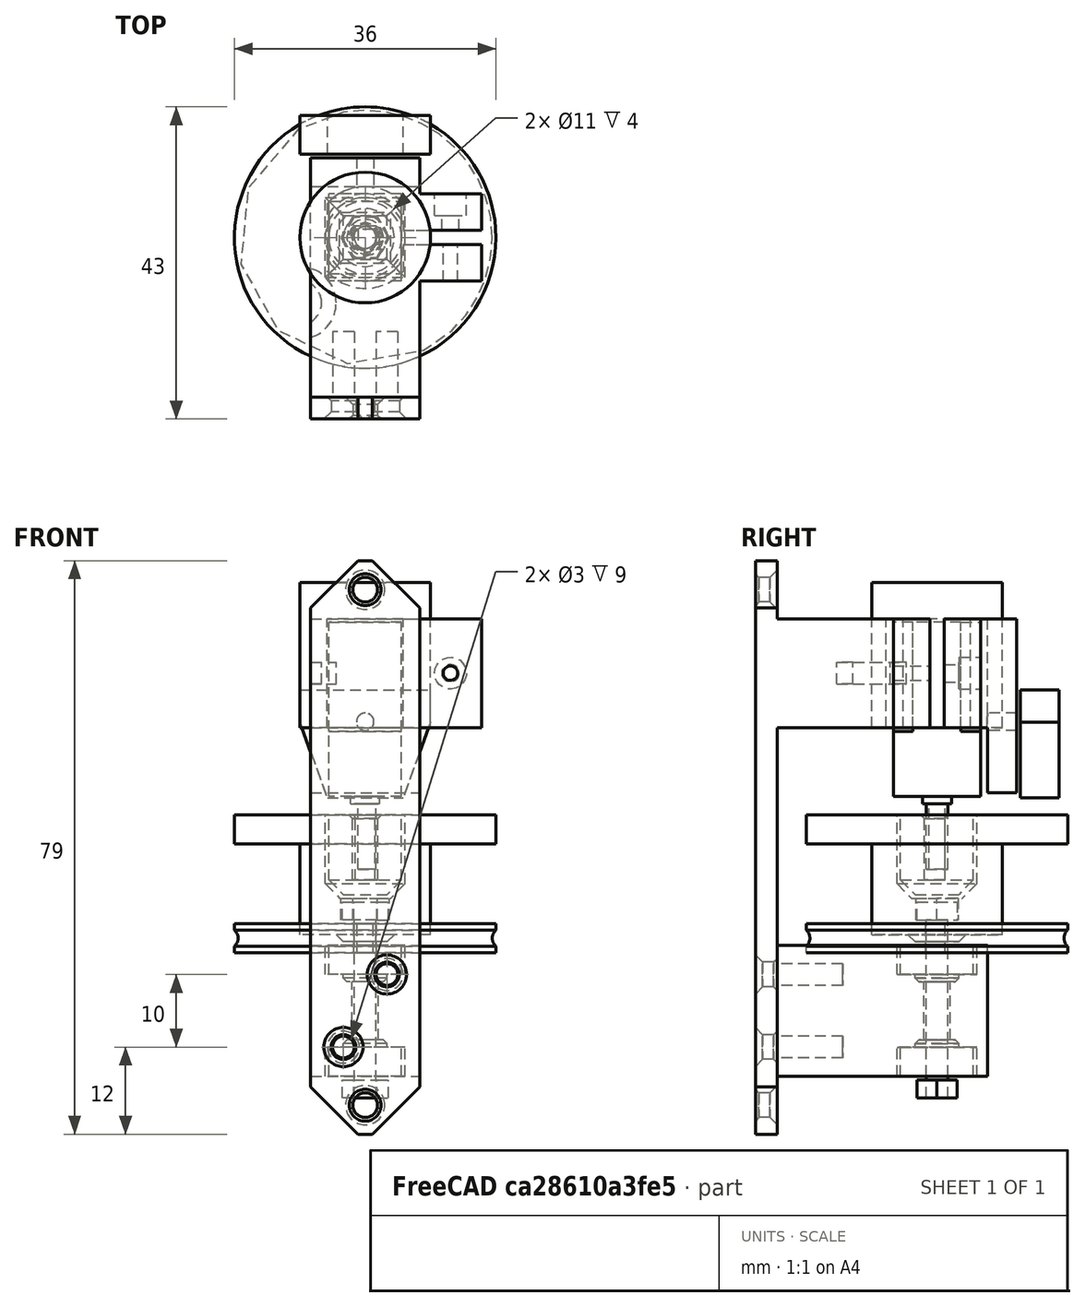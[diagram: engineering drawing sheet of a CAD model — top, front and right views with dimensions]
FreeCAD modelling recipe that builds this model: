
FCSTD DOCUMENT  (FreeCAD 0.18R16146 (Git))
Label: Motor and Opto Sensor Mount0.2
License: All rights reserved
LicenseURL: http://en.wikipedia.org/wiki/All_rights_reserved
objects: Part::Cylinder×31, Part::Cut×23, Part::Box×19, Part::MultiFuse×13, Part::Chamfer×10, Drawing::FeatureViewAnnotation×4, Part::Feature×3, Part::Fuse×3, Part::MultiCommon×2, Part::Torus×1, Part::Mirroring×1, Part::Cone×1, Drawing::FeaturePage×1
note: 107 computed .brp shape members not serialized (recipe doc carries the construction recipe); baked Part::Feature solids carry a one-line shape summary decoded from their .brp

FEATURE [Part::Box] Box406008004  label="gearbox004"
  AttacherType = Attacher::AttachEngine3D
  Height = 9
  Length = 12
  Placement = pos=(-6,-5,0) rot=(0,0,1;0rad)
  Width = 10
FEATURE [Part::Cylinder] Cylinder076  label="boss002"
  Angle = 360
  AttacherType = Attacher::AttachEngine3D
  Height = 1
  Placement = pos=(0,0,-1) rot=(0,0,1;0rad)
  Radius = 2
FEATURE [Part::Cylinder] Cylinder077
  Angle = 360
  AttacherType = Attacher::AttachEngine3D
  Height = 15
  Placement = pos=(0,0,9) rot=(0,0,1;0rad)
  Radius = 6
FEATURE [Part::Box] Box406008005  label="gearbox005"
  AttacherType = Attacher::AttachEngine3D
  Height = 27
  Length = 16
  Placement = pos=(-8,-5,0) rot=(0,0,1;0rad)
  Width = 10
FEATURE [Part::MultiCommon] Common001  label="motor002"
  Shapes = -> [Cylinder077,Box406008005]
FEATURE [Part::Cylinder] Cylinder078  label="shaft-002"
  Angle = 360
  AttacherType = Attacher::AttachEngine3D
  Height = 10
  Placement = pos=(0,0,-10) rot=(0,0,1;0rad)
  Radius = 1.5
FEATURE [Part::Box] Box406008006  label="Cube341"
  AttacherType = Attacher::AttachEngine3D
  Height = 12
  Length = 10
  Placement = pos=(-5,1,-11) rot=(0,0,1;0rad)
  Width = 10
FEATURE [Part::Cut] Cut001  label="shaft002"
  Base = -> Cylinder078
  Tool = -> Box406008006
FEATURE [Part::MultiFuse] Fusion103077013004017004  label="motor-assembled"
  Placement = pos=(0,0,20.5) rot=(0,0,1;1.5708rad)
  Shapes = -> [Box406008004,Cylinder076,Common001,Cut001]
FEATURE [Part::Cylinder] Cylinder028  label="Cylinder024"
  Angle = 360
  AttacherType = Attacher::AttachEngine3D
  Height = 10
  Placement = pos=(0,0,-1) rot=(0,0,1;0rad)
  Radius = 1.57
FEATURE [Part::Cylinder] Cylinder012  label="wheel1a"
  Angle = 360
  AttacherType = Attacher::AttachEngine3D
  Height = 4
  Radius = 18
FEATURE [Part::Box] Box084016  label="Cube067"
  AttacherType = Attacher::AttachEngine3D
  Height = 12
  Length = 10
  Placement = pos=(-5,1.1,-1.5) rot=(0,0,1;0rad)
  Width = 10
FEATURE [Part::Torus] Torus002
  Angle1 = -180
  Angle2 = 180
  Angle3 = 360
  AttacherType = Attacher::AttachEngine3D
  Placement = pos=(0,0,2) rot=(0,0,1;0rad)
  Radius1 = 19
  Radius2 = 1.5
FEATURE [Part::Cut] Cut057
  Base = -> Cylinder028
  Tool = -> Box084016
FEATURE [Part::Cut] Cut062
  Base = -> Cylinder012
  Tool = -> Cut057
FEATURE [Part::Cut] Cut063  label="wheel 0.1"
  Base = -> Cut062
  Placement = pos=(0,0,-1) rot=(0,0,1;0rad)
  Tool = -> Torus002
FEATURE [Part::Cylinder] Cylinder073  label="motor-bulge"
  Angle = 360
  AttacherType = Attacher::AttachEngine3D
  Height = 20
  Placement = pos=(0,0,30) rot=(0,0,1;0rad)
  Radius = 9
FEATURE [Part::Cylinder] Cylinder067
  Angle = 360
  AttacherType = Attacher::AttachEngine3D
  Height = 26
  Placement = pos=(0,0,20) rot=(0,0,1;0rad)
  Radius = 7
FEATURE [Part::Box] Box406017  label="gearbox001"
  AttacherType = Attacher::AttachEngine3D
  Height = 28
  Length = 16
  Placement = pos=(-8,-5.25,18) rot=(0,0,1;0rad)
  Width = 10.5
FEATURE [Part::MultiCommon] Common004  label="motor-hole"
  Placement = pos=(0,0,5) rot=(0,0,1;1.5708rad)
  Shapes = -> [Cylinder067,Box406017]
FEATURE [Part::Box] Box406016  label="clamp-slot"
  AttacherType = Attacher::AttachEngine3D
  Height = 32
  Length = 49
  Placement = pos=(48.48,1,22) rot=(0,0,1;3.14159rad)
  Width = 2
FEATURE [Part::Box] Box  label="Cube"
  AttacherType = Attacher::AttachEngine3D
  Height = 8
  Length = 15
  Placement = pos=(-7.5,-25,45) rot=(0,0,1;0rad)
  Width = 3
FEATURE [Part::Box] Box406008007  label="Cube342"
  AttacherType = Attacher::AttachEngine3D
  Height = 14.9
  Length = 18
  Placement = pos=(-9,13,34.3) rot=(0,0,1;0rad)
  Width = 5.3
FEATURE [Part::Cylinder] Cylinder079  label="Cylinder078"
  Angle = 360
  AttacherType = Attacher::AttachEngine3D
  Height = 17
  Placement = pos=(0,0,9) rot=(0,0,1;0rad)
  Radius = 1.75
FEATURE [Part::Box] Box406008008  label="Cube343"
  AttacherType = Attacher::AttachEngine3D
  Height = 19
  Length = 10
  Placement = pos=(-5,1.1,1.5) rot=(0,0,1;0rad)
  Width = 10
FEATURE [Part::Cut] Cut064  label="Motor Shaft Hole"
  Base = -> Cylinder079
  Tool = -> Box406008008
FEATURE [Part::Box] Box406008009  label="Cube344"
  AttacherType = Attacher::AttachEngine3D
  Height = 11
  Length = 10
  Placement = pos=(-5,-5,7) rot=(0,0,1;0rad)
  Width = 10
FEATURE [Part::Box] Box406008010  label="Cube345"
  AttacherType = Attacher::AttachEngine3D
  Height = 19.7
  Length = 17.5
  Placement = pos=(3.75,6,30.3) rot=(0,1,0;0.349066rad)
  Width = 13.3
FEATURE [Part::Box] Box406008011  label="Cube346"
  AttacherType = Attacher::AttachEngine3D
  Height = 19.7
  Length = 17.5
  Placement = pos=(3.75,6,30.3) rot=(0,1,0;0.349066rad)
  Width = 13.3
FEATURE [Part::Mirroring] Part__Mirroring  label="Cube346 (Mirror #1)"
  Base = (0,0,0)
  Normal = (1,0,0)
  Source = -> Box406008011
FEATURE [Part::MultiFuse] Fusion
  Shapes = -> [Box406008010,Part__Mirroring]
FEATURE [Part::Cut] Cut  label="Opto Sensor"
  Base = -> Box406008007
  Placement = pos=(0,-1.5,-14) rot=(0,0,1;0rad)
  Tool = -> Fusion
FEATURE [Part::Cut] Cut065  label="Square Peg"
  Base = -> Box406008009
  Tool = -> Cut064
FEATURE [Part::Box] Box406008012  label="Cube347"
  AttacherType = Attacher::AttachEngine3D
  Height = 11.5
  Length = 11
  Placement = pos=(-5.5,-5.5,6.5) rot=(0,0,1;0rad)
  Width = 11
FEATURE [Part::Cylinder] Cylinder
  Angle = 360
  AttacherType = Attacher::AttachEngine3D
  Height = 12.5
  Placement = pos=(0,0,1.5) rot=(0,0,1;0rad)
  Radius = 9
FEATURE [Part::Cylinder] Cylinder080  label="wheel1a001"
  Angle = 360
  AttacherType = Attacher::AttachEngine3D
  Height = 4
  Placement = pos=(0,0,14) rot=(0,0,1;0rad)
  Radius = 18
FEATURE [Part::Feature] Shape
  Placement = pos=(0,0,3.5) rot=(0,0,1;0rad)
  shape: bbox 6.697 x 5.8 x 15 mm, 8 faces (baked)
FEATURE [Part::MultiFuse] Fusion103077013004017005
  Shapes = -> [Cylinder080,Cylinder]
FEATURE [Part::Feature] Shape001
  Placement = pos=(0,0,3.5) rot=(0,0,1;0rad)
  shape: bbox 6.351 x 5.5 x 2.5 mm, 8 faces (baked)
FEATURE [Part::Cylinder] Cylinder081  label="Cylinder079"
  Angle = 360
  AttacherType = Attacher::AttachEngine3D
  Height = 25
  Placement = pos=(0,0,-21) rot=(0,0,1;0rad)
  Radius = 1.5
FEATURE [Part::MultiFuse] Fusion103077013004017006  label="M3 x 25 Hex Head"
  Shapes = -> [Shape001,Cylinder081]
FEATURE [Part::Cut] Cut066
  Base = -> Fusion103077013004017005
  Tool = -> Box406008012
FEATURE [Part::Cone] Cone
  Angle = 360
  AttacherType = Attacher::AttachEngine3D
  Height = 1
  Placement = pos=(0,0,0.5) rot=(0,0,1;0rad)
  Radius1 = 3
  Radius2 = 4
FEATURE [Part::MultiFuse] Fusion103077013004017007
  Shapes = -> [Cut066,Cone]
FEATURE [Part::Cut] Cut067
  Base = -> Fusion103077013004017007
  Tool = -> Shape
FEATURE [Part::Cylinder] Cylinder082  label="623 Bearing"
  Angle = 360
  AttacherType = Attacher::AttachEngine3D
  Height = 4
  Placement = pos=(0,0,-4) rot=(0,0,1;0rad)
  Radius = 5
FEATURE [Part::Cylinder] Cylinder083  label="623 Bearing001"
  Angle = 360
  AttacherType = Attacher::AttachEngine3D
  Height = 4
  Placement = pos=(0,0,-18) rot=(0,0,1;0rad)
  Radius = 5
FEATURE [Part::Feature] Shape002  label="Nylock"
  Placement = pos=(0,0,-21) rot=(0,0,1;0rad)
  shape: bbox 6.351 x 5.5 x 2.5 mm, 8 faces (baked)
FEATURE [Part::Cylinder] Cylinder084  label="Cylinder080"
  Angle = 360
  AttacherType = Attacher::AttachEngine3D
  Height = 6
  Placement = pos=(0,0,-2) rot=(0,0,1;0rad)
  Radius = 1.5
FEATURE [Part::Cut] Cut069
  Base = -> Cut067
  Tool = -> Cylinder084
FEATURE [Part::Cylinder] Cylinder085  label="Cylinder081"
  Angle = 360
  AttacherType = Attacher::AttachEngine3D
  Height = 12
  Placement = pos=(0,0,-14) rot=(0,0,1;0rad)
  Radius = 1.8
FEATURE [Part::Box] Box406008013  label="Cube348"
  AttacherType = Attacher::AttachEngine3D
  Height = 18
  Length = 15
  Placement = pos=(-7.5,-22,-18) rot=(0,0,1;0rad)
  Width = 29
FEATURE [Part::Cylinder] Cylinder086  label="623 Bearing002"
  Angle = 360
  AttacherType = Attacher::AttachEngine3D
  Height = 4
  Placement = pos=(0,0,-4) rot=(0,0,1;0rad)
  Radius = 5.5
FEATURE [Part::Cylinder] Cylinder087  label="623 Bearing003"
  Angle = 360
  AttacherType = Attacher::AttachEngine3D
  Height = 4
  Placement = pos=(0,0,-18) rot=(0,0,1;0rad)
  Radius = 5.5
FEATURE [Part::MultiFuse] Fusion103077013004017008  label="623 Bearing Holes"
  Shapes = -> [Cylinder086,Cylinder087]
FEATURE [Part::Cut] Cut070
  Base = -> Box406008013
  Tool = -> Fusion103077013004017008
FEATURE [Part::Cylinder] Cylinder088  label="Cylinder082"
  Angle = 360
  AttacherType = Attacher::AttachEngine3D
  Height = 1
  Placement = pos=(0,0,-5) rot=(0,0,1;0rad)
  Radius = 3
FEATURE [Part::Cylinder] Cylinder089  label="Cylinder083"
  Angle = 360
  AttacherType = Attacher::AttachEngine3D
  Height = 1
  Placement = pos=(0,0,-14) rot=(0,0,1;0rad)
  Radius = 3
FEATURE [Part::MultiFuse] Fusion103077013004017009
  Shapes = -> [Cylinder089,Cylinder088]
FEATURE [Part::Cut] Cut071
  Base = -> Cut070
  Tool = -> Fusion103077013004017009
FEATURE [Part::Cut] Cut072
  Base = -> Cut071
  Tool = -> Cylinder085
FEATURE [Part::Chamfer] Chamfer
  Base = -> Cut072
  Edges = 1 edges r=0.5: [Edge22]
FEATURE [Part::Chamfer] Chamfer001  label="Bearing Mount end"
  Base = -> Chamfer
  Edges = 1 edges r=0.5: [Edge16]
FEATURE [Part::Box] Box406008014  label="Cube349"
  AttacherType = Attacher::AttachEngine3D
  Height = 63
  Length = 15
  Placement = pos=(-7.5,-25,-18) rot=(0,0,1;0rad)
  Width = 3
FEATURE [Part::Box] Box406008015  label="Cube350"
  AttacherType = Attacher::AttachEngine3D
  Height = 15
  Length = 15
  Placement = pos=(-7.5,-22,35) rot=(0,0,1;0rad)
  Width = 31
FEATURE [Part::Cut] Cut073
  Base = -> Box406008015
  Tool = -> Common004
FEATURE [Part::Cylinder] Cylinder068
  Angle = 360
  AttacherType = Attacher::AttachEngine3D
  Height = 12
  Placement = pos=(11.75,0,42.5) rot=(0,0.707106,0.707107;3.14159rad)
  Radius = 1.2
FEATURE [Part::Cylinder] Cylinder069
  Angle = 360
  AttacherType = Attacher::AttachEngine3D
  Height = 12
  Placement = pos=(11.75,3,42.5) rot=(0,0.707106,0.707107;3.14159rad)
  Radius = 2.2
FEATURE [Part::MultiFuse] Fusion103077013  label="M2-screw001"
  Shapes = -> [Cylinder068,Cylinder069]
FEATURE [Part::Box] Box406008016  label="Cube351"
  AttacherType = Attacher::AttachEngine3D
  Height = 15
  Length = 9
  Placement = pos=(7,-6,35) rot=(0,0,1;0rad)
  Width = 12
FEATURE [Part::Fuse] Fusion103077013004017010
  Base = -> Cut073
  Tool = -> Box406008016
FEATURE [Part::Cut] Cut074
  Base = -> Fusion103077013004017010
  Tool = -> Box406016
FEATURE [Part::Box] Box406008017  label="Cube352"
  AttacherType = Attacher::AttachEngine3D
  Height = 24
  Length = 15
  Placement = pos=(-7.5,7,26) rot=(0,0,1;0rad)
  Width = 4
FEATURE [Part::Cylinder] Cylinder090  label="Cylinder084"
  Angle = 360
  AttacherType = Attacher::AttachEngine3D
  Height = 13
  Placement = pos=(0,16,35.8) rot=(1,0,0;1.5708rad)
  Radius = 1.2
FEATURE [Part::Cylinder] Cylinder091
  Angle = 360
  AttacherType = Attacher::AttachEngine3D
  Height = 12
  Placement = pos=(11.75,-12,42.5) rot=(0,0.707106,0.707107;3.14159rad)
  Radius = 1
FEATURE [Part::Fuse] Fusion103077013004017011
  Base = -> Fusion103077013
  Tool = -> Cylinder091
FEATURE [Part::Cut] Cut075
  Base = -> Cut074
  Tool = -> Fusion103077013004017011
FEATURE [Part::Fuse] Fusion103077013004017012
  Base = -> Box406008017
  Tool = -> Cut075
FEATURE [Part::Cut] Cut076  label="Motor Mount 0.2"
  Base = -> Fusion103077013004017012
  Placement = pos=(0,0,-5) rot=(0,0,1;0rad)
  Tool = -> Cylinder090
FEATURE [Part::Cylinder] Cylinder092
  Angle = 360
  AttacherType = Attacher::AttachEngine3D
  Height = 21
  Placement = pos=(-3,-13,-14) rot=(1,0,0;1.5708rad)
  Radius = 1.7
FEATURE [Part::Cylinder] Cylinder093
  Angle = 360
  AttacherType = Attacher::AttachEngine3D
  Height = 21
  Placement = pos=(3,-13,-4) rot=(1,0,0;1.5708rad)
  Radius = 1.7
FEATURE [Part::Cylinder] Cylinder094
  Angle = 360
  AttacherType = Attacher::AttachEngine3D
  Height = 21
  Placement = pos=(-3,-13,-14) rot=(1,0,0;1.5708rad)
  Radius = 1.5
FEATURE [Part::Cylinder] Cylinder095
  Angle = 360
  AttacherType = Attacher::AttachEngine3D
  Height = 21
  Placement = pos=(3,-13,-4) rot=(1,0,0;1.5708rad)
  Radius = 1.5
FEATURE [Part::MultiFuse] Fusion103077013004017013
  Shapes = -> [Cylinder092,Cylinder093]
FEATURE [Part::Cut] Cut077
  Base = -> Box406008014
  Tool = -> Fusion103077013004017013
FEATURE [Part::MultiFuse] Fusion103077013004017014
  Shapes = -> [Cylinder094,Cylinder095]
FEATURE [Part::Cut] Cut078  label="Bearing Mount End 0.2"
  Base = -> Chamfer001
  Tool = -> Fusion103077013004017014
FEATURE [Part::Cylinder] Cylinder096
  Angle = 360
  AttacherType = Attacher::AttachEngine3D
  Height = 21
  Placement = pos=(0,-13,49) rot=(1,0,0;1.5708rad)
  Radius = 1.7
FEATURE [Part::Cylinder] Cylinder097
  Angle = 360
  AttacherType = Attacher::AttachEngine3D
  Height = 21
  Placement = pos=(0,-13,-22) rot=(1,0,0;1.5708rad)
  Radius = 1.7
FEATURE [Part::Chamfer] Chamfer003  label="Wheel"
  Base = -> Cut069
  Edges = 4 edges r=2: [Edge11,Edge12,Edge15,Edge16]
FEATURE [Part::Chamfer] Chamfer004  label="Square Peg001"
  Base = -> Cut065
  Edges = 4 edges r=2: [Edge4,Edge5,Edge13,Edge15]
FEATURE [Part::Box] Box406008018  label="Cube353"
  AttacherType = Attacher::AttachEngine3D
  Height = 8
  Length = 15
  Placement = pos=(-7.5,-25,-26) rot=(0,0,1;0rad)
  Width = 3
FEATURE [Part::Cut] Cut079
  Base = -> Box406008018
  Tool = -> Cylinder097
FEATURE [Part::Cut] Cut080
  Base = -> Box
  Tool = -> Cylinder096
FEATURE [Part::MultiFuse] Fusion103077013004017015
  Shapes = -> [Cut079,Cut080]
FEATURE [Part::Chamfer] Chamfer005
  Base = -> Fusion103077013004017015
  Edges = 2 edges r=1: [Edge13,Edge28]
FEATURE [Part::Chamfer] Chamfer006
  Base = -> Cut077
  Edges = 2 edges r=1: [Edge8,Edge9]
FEATURE [Part::MultiFuse] Fusion103077013004017016
  Shapes = -> [Chamfer006,Chamfer005]
FEATURE [Part::Chamfer] Chamfer007
  Base = -> Fusion103077013004017016
  Edges = 4 edges r=6.5: [Edge27,Edge29,Edge34,Edge39]
FEATURE [Part::Cylinder] Cylinder098
  Angle = 360
  AttacherType = Attacher::AttachEngine3D
  Height = 3
  Placement = pos=(-9,-9,36) rot=(1,0,0;0rad)
  Radius = 5
FEATURE [Part::Cylinder] Cylinder099
  Angle = 360
  AttacherType = Attacher::AttachEngine3D
  Height = 3
  Placement = pos=(-9,-9,36) rot=(1,0,0;0rad)
  Radius = 3
FEATURE [Part::Cut] Cut081
  Base = -> Cylinder098
  Tool = -> Cylinder099
FEATURE [Part::Cut] Cut082
  Base = -> Cut076
  Tool = -> Cut081
FEATURE [Part::MultiFuse] Fusion103077013004017017
  Shapes = -> [Chamfer007,Cut082]
FEATURE [Drawing::FeatureViewAnnotation] Annotation
  Font = Sans
  Rotation = 0
  Scale = 7
  Text = Square Peg 0.1 - 0.2 Hole R 1.57 -> 1.75 and chamfered
  ViewResult = <g transform="translate(10,20) rotate(0)">\n<text id="Annotation"\n font-family="Sans"\n font-size="7"\n fill="#000000">\n<tspan x="0" dy="1em">Square Peg 0.1 - 0.2 Hole R 1.57 -> 1.75 and chamfered</tspan>\n</text>\n</g>
  Visible = true
  X = 10
  Y = 20
FEATURE [Part::Chamfer] Chamfer008  label="Square Peg 0.2"
  Base = -> Chamfer004
  Edges = 3 edges r=0.5: [Edge13,Edge14,Edge15]
FEATURE [Drawing::FeatureViewAnnotation] Annotation001
  Font = Sans
  Rotation = 0
  Scale = 7
  Text = Bearing Mount End 0.2 0 Hole R 1.5 -> 1.8
  ViewResult = <g transform="translate(10,60) rotate(0)">\n<text id="Annotation001"\n font-family="Sans"\n font-size="7"\n fill="#000000">\n<tspan x="0" dy="1em">Bearing Mount End 0.2 0 Hole R 1.5 -> 1.8</tspan>\n</text>\n</g>
  Visible = true
  X = 10
  Y = 60
FEATURE [Drawing::FeatureViewAnnotation] Annotation002
  Font = Sans
  Rotation = 0
  Scale = 7
  Text = Motor Mount Hole 6.25 -> 7mm
  ViewResult = <g transform="translate(10,40) rotate(0)">\n<text id="Annotation002"\n font-family="Sans"\n font-size="7"\n fill="#000000">\n<tspan x="0" dy="1em">Motor Mount Hole 6.25 -> 7mm</tspan>\n</text>\n</g>
  Visible = true
  X = 10
  Y = 40
FEATURE [Part::Chamfer] Chamfer009
  Base = -> Fusion103077013004017017
  Edges = 2 edges r=0.5: [Edge46,Edge47]
FEATURE [Part::Chamfer] Chamfer010  label="Motor and Opto Sensor Mount 0.2"
  Base = -> Chamfer009
  Edges = 2 edges r=0.5: [Edge102,Edge107]
FEATURE [Drawing::FeatureViewAnnotation] Annotation003
  Font = Sans
  Rotation = 0
  Scale = 7
  Text = Chamfered holes that are printed sideways
  ViewResult = <g transform="translate(10,80) rotate(0)">\n<text id="Annotation003"\n font-family="Sans"\n font-size="7"\n fill="#000000">\n<tspan x="0" dy="1em">Chamfered holes that are printed sideways</tspan>\n</text>\n</g>
  Visible = true
  X = 10
  Y = 80
FEATURE [Drawing::FeaturePage] Page
  EditableTexts = AUTHOR NAME | CREATION DATE | SUPERVISOR NAME | CHECK DATE | SCALE | WEIGHT | NUMBER | SHEET | TITLE | SUBTITLE
  Group = -> [Annotation,Annotation001,Annotation002,Annotation003]
  Template = <path>
note: 1 file-system path scrubbed to <path> (originals preserved in the JSON sidecar)
